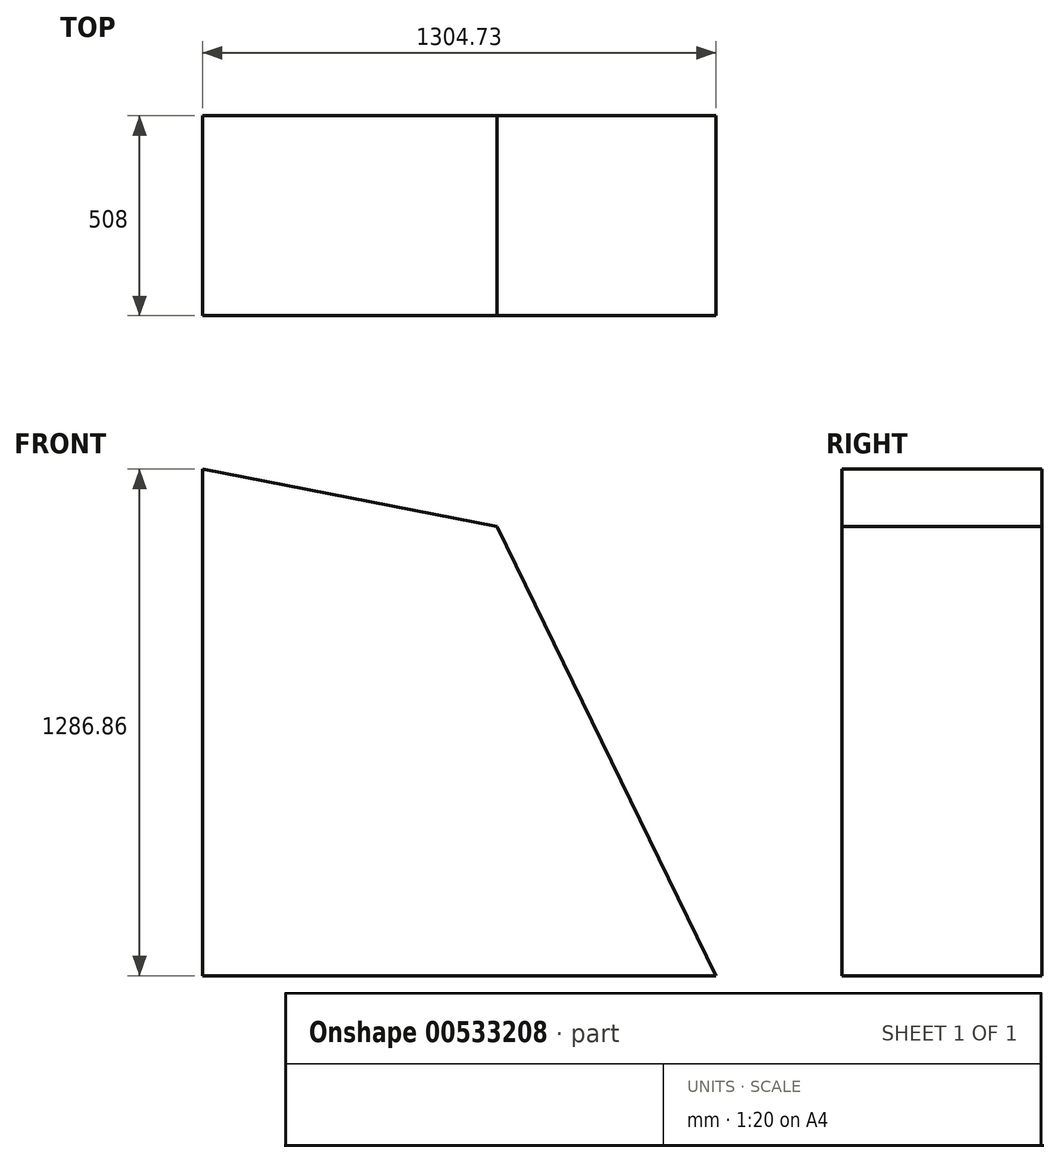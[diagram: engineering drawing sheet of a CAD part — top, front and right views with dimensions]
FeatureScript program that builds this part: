
annotation { "Feature Type Name" : "Feature", "Feature Type Description" : "" }
export const myFeature = defineFeature(function(context is Context, id is Id, definition is map)
    precondition{}
    {
        {
            var Q0;
            Q0=qCreatedBy(makeId("Front.planeOp"),FACE);
            var sketch = newSketch(context, id + "F0", { "sketchPlane" : qUnion([Q0])});
            skLineSegment(sketch, "E0", {"start": v(0, 0) * mm, "end": v(748, -145.4) * mm});
            skLineSegment(sketch, "E1", {"start": v(748, -145.4) * mm, "end": v(1304.73, -1286.86) * mm});
            skLineSegment(sketch, "E2", {"start": v(1304.73, -1286.86) * mm, "end": v(0, -1286.86) * mm});
            skLineSegment(sketch, "E3", {"start": v(0, -1286.86) * mm, "end": v(0, 0) * mm});
            skSolve(sketch);
        }
        {
            var Q0;
            Q0 = qSketchRegion(id + "F0", true);
            var Q1;
            Q1=makeQuery(id+"F0.imprint","IMPRINT",FACE,{"disambiguationData":[TD([[makeQuery(id+"F0.imprint","IMPRINT",EDGE,{"derivedFrom":sQuery(id+"F0.wireOp",EDGE,"E0")}),-1.0]])]});
            extrude(context, id + "F1", {"entities" : qUnion([Q0, Q1]), "depth" : 508 * mm, "offsetDistance" : 25.4 * mm});
        }
    });
